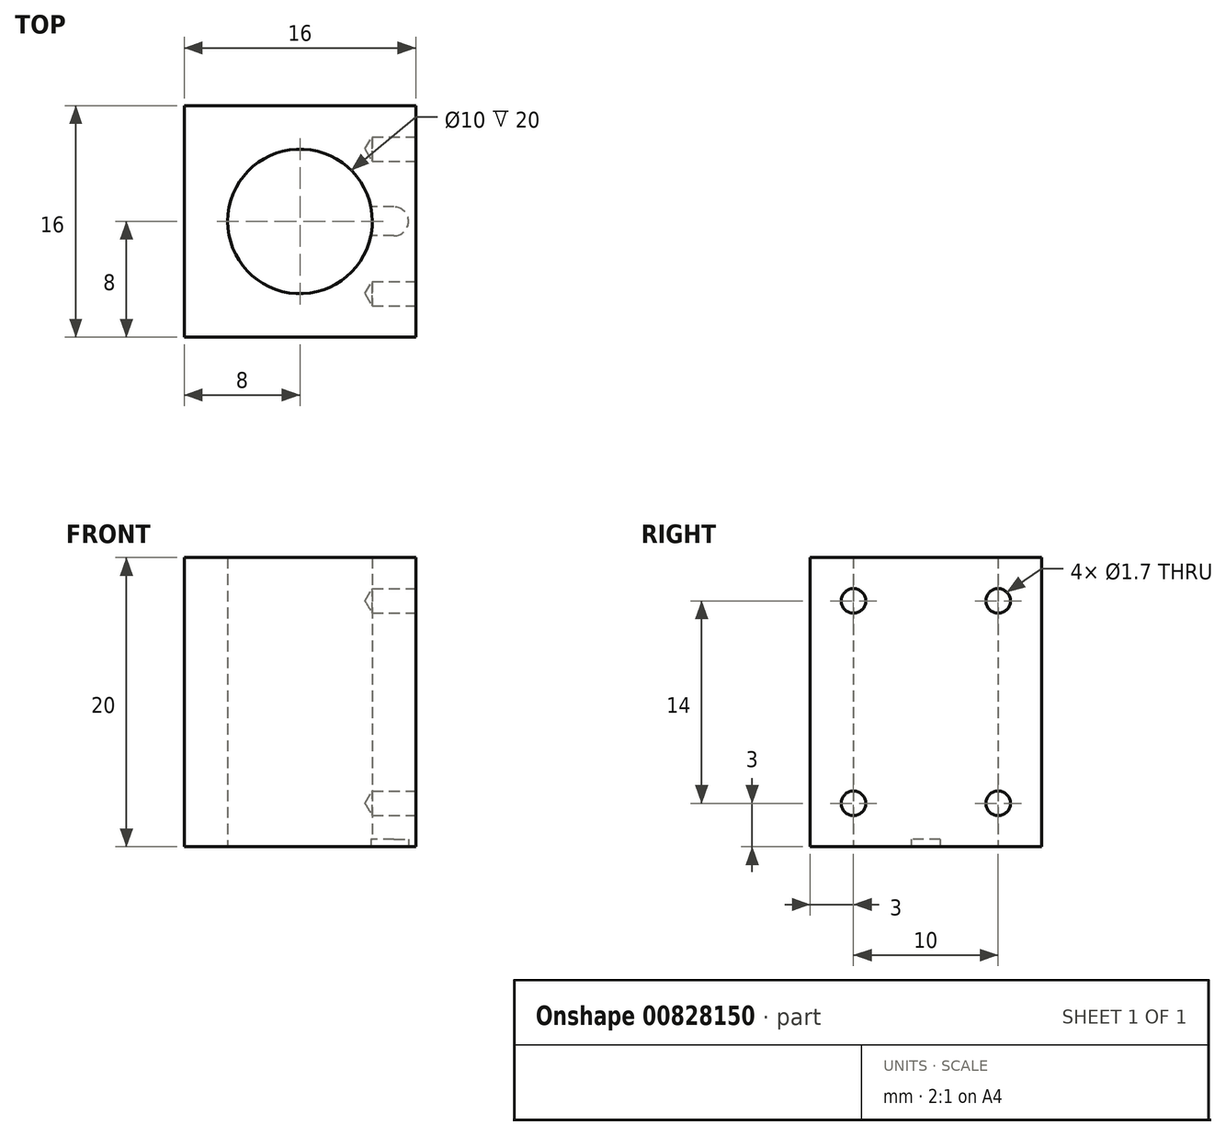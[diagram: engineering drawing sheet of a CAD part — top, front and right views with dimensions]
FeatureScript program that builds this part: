
annotation { "Feature Type Name" : "Feature", "Feature Type Description" : "" }
export const myFeature = defineFeature(function(context is Context, id is Id, definition is map)
    precondition{}
    {
        {
            var Q0;
            Q0=qCreatedBy(makeId("Top.planeOp"),FACE);
            var sketch = newSketch(context, id + "F0", { "sketchPlane" : qUnion([Q0])});
            skLineSegment(sketch, "E0.bottom", {"start": v(8, 8) * mm, "end": v(-8, 8) * mm});
            skLineSegment(sketch, "E0.top", {"start": v(8, -8) * mm, "end": v(-8, -8) * mm});
            skLineSegment(sketch, "E0.left", {"start": v(8, 8) * mm, "end": v(8, -8) * mm});
            skLineSegment(sketch, "E0.right", {"start": v(-8, 8) * mm, "end": v(-8, -8) * mm});
            skPoint(sketch, "E0.middle", {"position": v(0, 0) * mm});
            skCircle(sketch, "E1", {"center": v(0, 0) * mm, "radius": 5 * mm});
            skSolve(sketch);
        }
        {
            var Q0;
            Q0 = qSketchRegion(id + "F0", true);
            extrude(context, id + "F1", {"entities" : qUnion([Q0]), "depth" : 20 * mm, "offsetDistance" : 25 * mm});
        }
        {
            var Q0;
            Q0=makeQuery(id+"F1.opExtrude","SWEPT_FACE",FACE,{"disambiguationData":[OSD([sQuery(id+"F0.wireOp",EDGE,"E0.left")])]});
            var sketch = newSketch(context, id + "F2", { "sketchPlane" : qUnion([Q0])});
            skCircle(sketch, "E2", {"center": v(-5, 3) * mm, "radius": 0.85 * mm});
            skCircle(sketch, "E3", {"center": v(5, 3) * mm, "radius": 0.85 * mm});
            skCircle(sketch, "E4", {"center": v(5, 17) * mm, "radius": 0.85 * mm});
            skCircle(sketch, "E5", {"center": v(-5, 17) * mm, "radius": 0.85 * mm});
            skSolve(sketch);
        }
        {
            var Q0;
            Q0=sQuery(id+"F2.wireOp",VERTEX,"E5.center");
            var Q1;
            Q1=sQuery(id+"F2.wireOp",VERTEX,"E4.center");
            var Q2;
            Q2=sQuery(id+"F2.wireOp",VERTEX,"E3.center");
            var Q3;
            Q3=sQuery(id+"F2.wireOp",VERTEX,"E2.center");
            var Q4;
            Q4=makeQuery(id+"F1.opExtrude","SWEPT_BODY",BODY,{"disambiguationData":[OSD([sQuery(id+"F0.wireOp",EDGE,"E0.bottom"),sQuery(id+"F0.wireOp",EDGE,"E0.top"),sQuery(id+"F0.wireOp",EDGE,"E0.left"),sQuery(id+"F0.wireOp",EDGE,"E0.right"),sQuery(id+"F0.wireOp",EDGE,"E1")])]});
            hole(context, id + "F3", {"style" : HoleStyle.SIMPLE, "endStyle" : HoleEndStyle.BLIND, "holeDiameter" : 1.7 * mm, "majorDiameter" : 5 * mm, "holeDepth" : 3 * mm, "isTappedThrough" : true, "tappedDepth" : 7.3 * mm, "tapClearance" : 3, "locations" : qUnion([Q0, Q1, Q2, Q3]), "scope" : qUnion([Q4])});
        }
        {
            var Q0;
            Q0=makeQuery(id+"F1.opExtrude","CAP_FACE",FACE,{"disambiguationData":[OSD([sQuery(id+"F0.wireOp",EDGE,"E0.bottom"),sQuery(id+"F0.wireOp",EDGE,"E0.top"),sQuery(id+"F0.wireOp",EDGE,"E0.left"),sQuery(id+"F0.wireOp",EDGE,"E0.right"),sQuery(id+"F0.wireOp",EDGE,"E1")])],"isStart":true});
            var sketch = newSketch(context, id + "F4", { "sketchPlane" : qUnion([Q0])});
            skLineSegment(sketch, "E6.bottom", {"start": v(6.5, -1) * mm, "end": v(0, -1) * mm});
            skLineSegment(sketch, "E6.top", {"start": v(6.5, 1) * mm, "end": v(0, 1) * mm});
            skLineSegment(sketch, "E6.right", {"start": v(0, -1) * mm, "end": v(0, 1) * mm});
            skPoint(sketch, "E6.middle", {"position": v(3.25, 0) * mm});
            skArc(sketch, "E7", {"start": v(6.5, -1) * mm, "mid": v(7.5, 0) * mm, "end": v(6.5, 1) * mm});
            skSolve(sketch);
        }
        {
            var Q0;
            Q0 = qSketchRegion(id + "F4", true);
            extrude(context, id + "F5", {"entities" : qUnion([Q0]), "operationType" : NewBodyOperationType.REMOVE, "oppositeDirection" : true, "depth" : 0.5 * mm, "offsetDistance" : 25 * mm});
        }
    });
